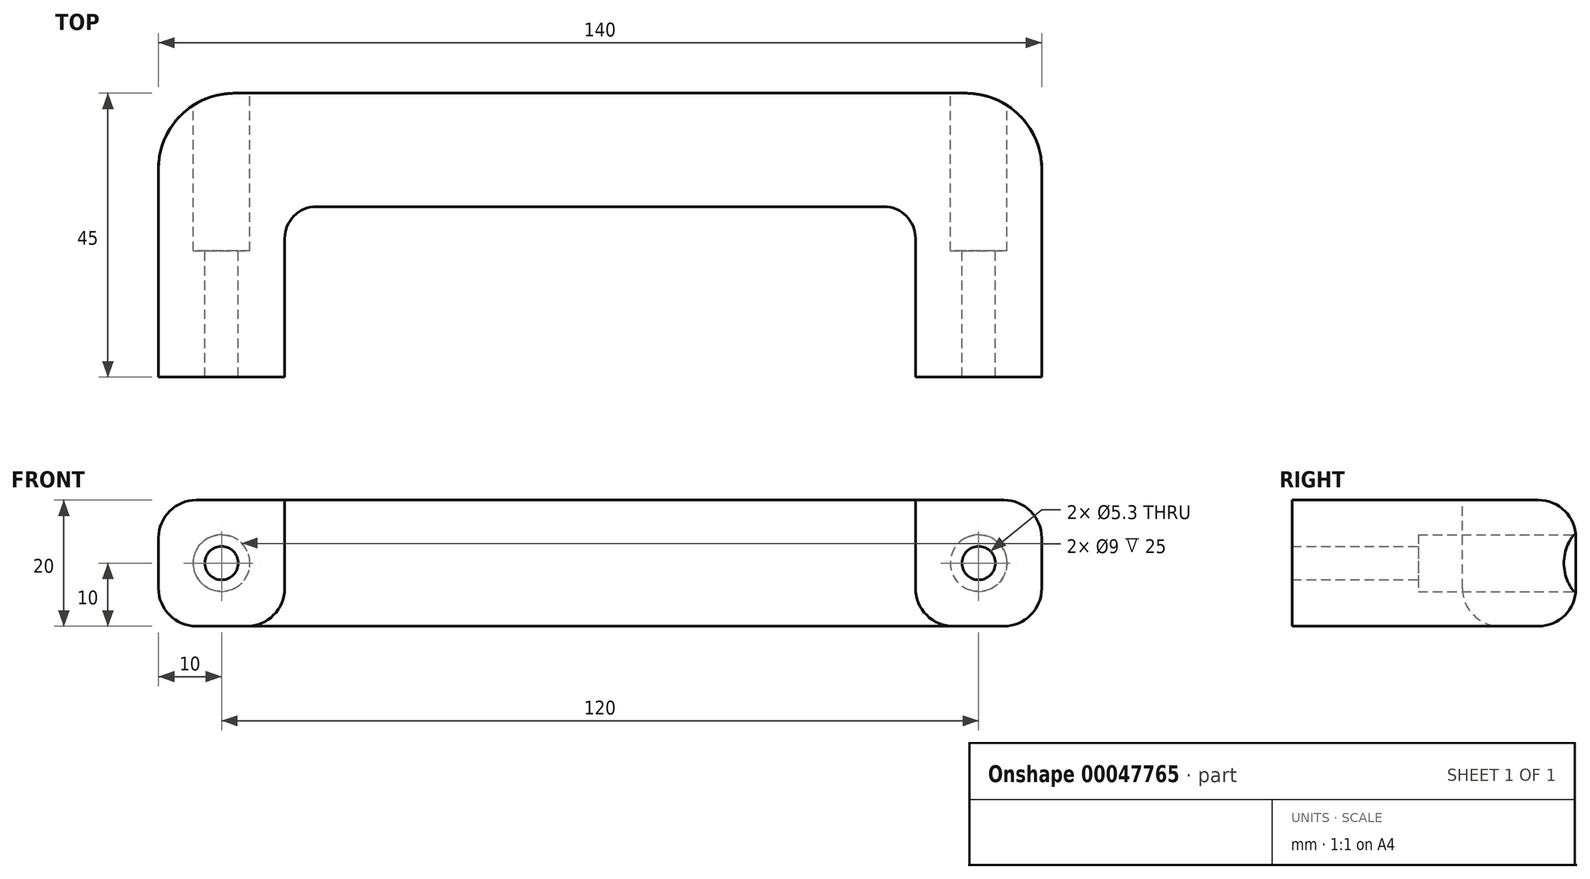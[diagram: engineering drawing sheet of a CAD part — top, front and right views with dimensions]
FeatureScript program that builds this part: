
annotation { "Feature Type Name" : "Feature", "Feature Type Description" : "" }
export const myFeature = defineFeature(function(context is Context, id is Id, definition is map)
    precondition{}
    {
        {
            var Q0;
            Q0=qCreatedBy(makeId("Top.planeOp"),FACE);
            var sketch = newSketch(context, id + "F0", { "sketchPlane" : qUnion([Q0])});
            skLineSegment(sketch, "E0.rect.bottom", {"start": v(-70, 22.5) * mm, "end": v(70, 22.5) * mm});
            skLineSegment(sketch, "E0.rect.top", {"start": v(-70, -22.5) * mm, "end": v(70, -22.5) * mm});
            skLineSegment(sketch, "E0.rect.left", {"start": v(-70, 22.5) * mm, "end": v(-70, -22.5) * mm});
            skLineSegment(sketch, "E0.rect.right", {"start": v(70, 22.5) * mm, "end": v(70, -22.5) * mm});
            skPoint(sketch, "E0.rect.middle", {"position": v(0, 0) * mm});
            skSolve(sketch);
        }
        {
            var Q0;
            Q0=makeQuery(id+"F0.imprint","IMPRINT",FACE,{"disambiguationData":[TD([[makeQuery(id+"F0.imprint","IMPRINT",EDGE,{"derivedFrom":sQuery(id+"F0.wireOp",EDGE,"E0.rect.bottom")}),-1.0]])]});
            extrude(context, id + "F1", {"entities" : qUnion([Q0]), "depth" : 20 * mm});
        }
        {
            var Q0;
            Q0=makeQuery(id+"F1.opExtrude","CAP_FACE",FACE,{"disambiguationData":[OSD([sQuery(id+"F0.wireOp",EDGE,"E0.rect.bottom"),sQuery(id+"F0.wireOp",EDGE,"E0.rect.top"),sQuery(id+"F0.wireOp",EDGE,"E0.rect.left"),sQuery(id+"F0.wireOp",EDGE,"E0.rect.right")])],"isStart":false});
            var sketch = newSketch(context, id + "F2", { "sketchPlane" : qUnion([Q0])});
            skLineSegment(sketch, "E1.bottom", {"start": v(-50, -22.5) * mm, "end": v(50, -22.5) * mm});
            skLineSegment(sketch, "E1.top", {"start": v(-50, 4.5) * mm, "end": v(50, 4.5) * mm});
            skLineSegment(sketch, "E1.left", {"start": v(-50, -22.5) * mm, "end": v(-50, 4.5) * mm});
            skLineSegment(sketch, "E1.right", {"start": v(50, -22.5) * mm, "end": v(50, 4.5) * mm});
            skSolve(sketch);
        }
        {
            var Q0;
            Q0=makeQuery(id+"F2.imprint","IMPRINT",FACE,{"disambiguationData":[TD([[makeQuery(id+"F2.imprint","IMPRINT",EDGE,{"derivedFrom":sQuery(id+"F2.wireOp",EDGE,"E1.bottom")}),1.0]])]});
            extrude(context, id + "F3", {"entities" : qUnion([Q0]), "operationType" : NewBodyOperationType.REMOVE, "oppositeDirection" : true, "depth" : 25 * mm});
        }
        {
            var Q0;
            Q0=makeQuery(id+"F1.opExtrude","SWEPT_FACE",FACE,{"disambiguationData":[OSD([sQuery(id+"F0.wireOp",EDGE,"E0.rect.bottom")])]});
            var sketch = newSketch(context, id + "F4", { "sketchPlane" : qUnion([Q0])});
            skCircle(sketch, "E2", {"center": v(60, 10) * mm, "radius": 2.65 * mm});
            skCircle(sketch, "E3", {"center": v(-60, 10) * mm, "radius": 2.65 * mm});
            skSolve(sketch);
        }
        {
            var Q0;
            Q0 = qSketchRegion(id + "F4", true);
            extrude(context, id + "F5", {"entities" : qUnion([Q0]), "operationType" : NewBodyOperationType.REMOVE, "endBound" : BoundingType.THROUGH_ALL, "oppositeDirection" : true, "depth" : 25 * mm});
        }
        {
            var Q0;
            Q0=makeQuery(id+"F1.opExtrude","SWEPT_FACE",FACE,{"disambiguationData":[OSD([sQuery(id+"F0.wireOp",EDGE,"E0.rect.bottom")])]});
            var sketch = newSketch(context, id + "F6", { "sketchPlane" : qUnion([Q0])});
            skCircle(sketch, "E4", {"center": v(60, 10) * mm, "radius": 4.5 * mm});
            skCircle(sketch, "E5", {"center": v(-60, 10) * mm, "radius": 4.5 * mm});
            skSolve(sketch);
        }
        {
            var Q0;
            Q0 = qSketchRegion(id + "F6", true);
            extrude(context, id + "F7", {"entities" : qUnion([Q0]), "operationType" : NewBodyOperationType.REMOVE, "oppositeDirection" : true, "depth" : 25 * mm});
        }
        {
            var Q0;
            Q0=makeQuery(id+"F1.opExtrude","SWEPT_EDGE",EDGE,{"disambiguationData":[OSD([sQuery(id+"F0.wireOp",EDGE,"E0.rect.bottom"),sQuery(id+"F0.wireOp",EDGE,"E0.rect.left")])]});
            var Q1;
            Q1=makeQuery(id+"F1.opExtrude","SWEPT_EDGE",EDGE,{"disambiguationData":[OSD([sQuery(id+"F0.wireOp",EDGE,"E0.rect.bottom"),sQuery(id+"F0.wireOp",EDGE,"E0.rect.right")])]});
            fillet(context, id + "F8", {"entities" : qUnion([Q0, Q1]), "radius" : 12 * mm, "tangentPropagation" : true, "allowEdgeOverflow" : false});
        }
        {
            var Q0;
            Q0=makeQuery(id+"F3.boolean.opBoolean","COPY",EDGE,{"derivedFrom":makeQuery(id+"F3.opExtrude","SWEPT_EDGE",EDGE,{"disambiguationData":[OSD([sQuery(id+"F2.wireOp",EDGE,"E1.top"),sQuery(id+"F2.wireOp",EDGE,"E1.left")])]})});
            var Q1;
            Q1=makeQuery(id+"F3.boolean.opBoolean","COPY",EDGE,{"derivedFrom":makeQuery(id+"F3.opExtrude","SWEPT_EDGE",EDGE,{"disambiguationData":[OSD([sQuery(id+"F2.wireOp",EDGE,"E1.top"),sQuery(id+"F2.wireOp",EDGE,"E1.right")])]})});
            fillet(context, id + "F9", {"entities" : qUnion([Q0, Q1]), "radius" : 5 * mm, "tangentPropagation" : true, "allowEdgeOverflow" : false});
        }
        {
            var Q0;
            Q0=makeQuery(id+"F1.opExtrude","CAP_EDGE",EDGE,{"disambiguationData":[OSD([sQuery(id+"F0.wireOp",EDGE,"E0.rect.bottom")])],"isStart":false});
            var Q1;
            Q1=makeQuery(id+"F1.opExtrude","CAP_EDGE",EDGE,{"disambiguationData":[OSD([sQuery(id+"F0.wireOp",EDGE,"E0.rect.bottom")])],"isStart":true});
            var Q2;
            Q2=makeQuery(id+"F3.boolean.opBoolean","COPY",EDGE,{"derivedFrom":makeQuery(id+"F3.opExtrude","CAP_EDGE",EDGE,{"disambiguationData":[OSD([sQuery(id+"F2.wireOp",EDGE,"E1.top")])],"isStart":true})});
            var Q3;
            Q3=makeQuery(id+"F3.boolean.opBoolean","INTERSECT",EDGE,{"derivedFrom":[makeQuery(id+"F1.opExtrude","CAP_FACE",FACE,{"disambiguationData":[OSD([sQuery(id+"F0.wireOp",EDGE,"E0.rect.bottom"),sQuery(id+"F0.wireOp",EDGE,"E0.rect.top"),sQuery(id+"F0.wireOp",EDGE,"E0.rect.left"),sQuery(id+"F0.wireOp",EDGE,"E0.rect.right")])],"isStart":true}),makeQuery(id+"F3.opExtrude","SWEPT_FACE",FACE,{"disambiguationData":[OSD([sQuery(id+"F2.wireOp",EDGE,"E1.top")])]})]});
            fillet(context, id + "F10", {"entities" : qUnion([Q0, Q1, Q2, Q3]), "radius" : 6 * mm, "tangentPropagation" : true, "allowEdgeOverflow" : false});
        }
    });
